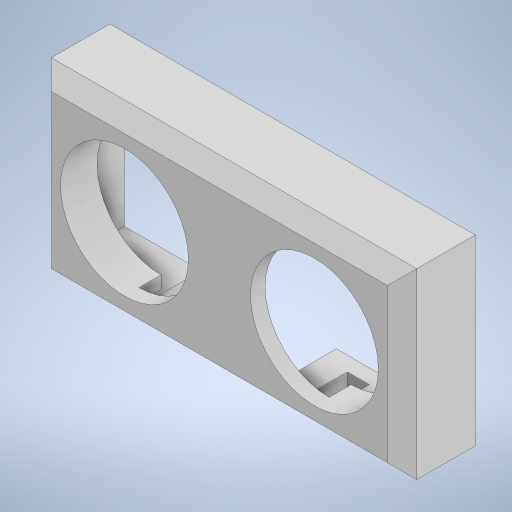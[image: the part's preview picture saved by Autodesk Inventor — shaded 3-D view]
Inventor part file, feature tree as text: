
AUTODESK INVENTOR PART (.ipt)
format: ipt  version: 2024.2 (Build 282272000, 272)  size: 298,496 bytes
history: native  units: mm
features: extrude x4, sketch x4, chamfer x1
ambient origin geometry x8: Origin, YZ Plane, XZ Plane, XY Plane, X Axis, Y Axis, Z Axis, Center Point
bodies: Solid1 (feature_tree)
feature tree (9):
  extrude  "Extrusion1"  Depth=17.5mm
  extrude  "Extrusion2"  Depth=50.0mm
  extrude  "Extrusion3"  Depth=12.0mm
  chamfer  "Chamfer2"  Distance=2.0mm
  extrude  "Extrusion4"  Depth=2.0mm
  sketch  "Sketch1"  dims[d0=17.5mm d1=17.5mm]
  sketch  "Sketch2"  dims[d2=26.0mm d3=50.0mm]
  sketch  "Sketch3"  dims[d4=25.0mm d5=12.0mm]
  sketch  "Sketch5"  dims[d6=12.5mm d7=2.0mm d8=0.0mm d12=2.0mm d14=46.0mm d15=2.0mm d16=21.0mm d17=8.0mm d18=0.0mm d19=12.0mm d20=19.0mm d21=2.0mm d22=2.0mm d23=25.0mm d24=3.0mm d25=0.0mm d26=2.0mm d27=2.0mm d28=45.0deg d29=3.0mm d31=3.0mm d33=19.0mm d34=12.5mm d35=1.5mm d36=3.0mm d37=0.0mm d38=2.0mm d39=1.5mm]
